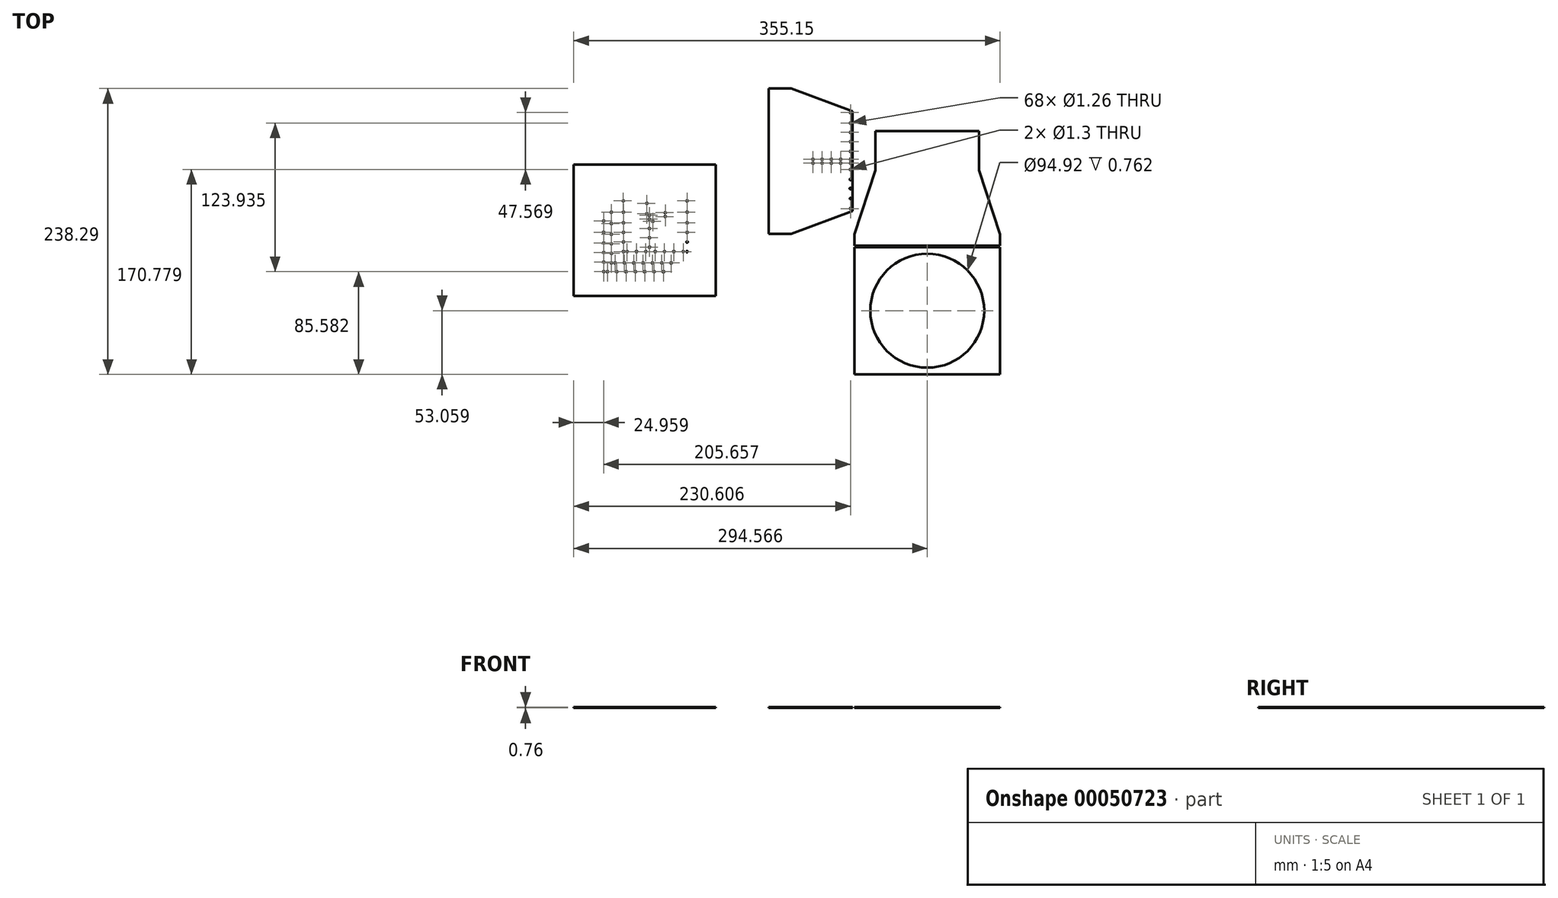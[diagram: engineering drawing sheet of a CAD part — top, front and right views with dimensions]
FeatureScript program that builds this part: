
annotation { "Feature Type Name" : "Feature", "Feature Type Description" : "" }
export const myFeature = defineFeature(function(context is Context, id is Id, definition is map)
    precondition{}
    {
        {
            var Q0;
            Q0=qCreatedBy(makeId("Top.planeOp"),FACE);
            var sketch = newSketch(context, id + "F0", { "sketchPlane" : qUnion([Q0])});
            skLineSegment(sketch, "E0", {"start": v(-23.3, 100.74) * mm, "end": v(-23.3, 17.43) * mm});
            skLineSegment(sketch, "E1", {"start": v(-93.15, 119.66) * mm, "end": v(-93.15, -1.5) * mm});
            skLineSegment(sketch, "E2", {"start": v(-74.2, -1.5) * mm, "end": v(-23.3, 17.43) * mm});
            skLineSegment(sketch, "E3", {"start": v(-74.2, 119.66) * mm, "end": v(-23.3, 100.74) * mm});
            skLineSegment(sketch, "E4", {"start": v(-21.54, -118.63) * mm, "end": v(99.62, -118.63) * mm});
            skLineSegment(sketch, "E5", {"start": v(-21.54, -12.5) * mm, "end": v(99.62, -12.5) * mm});
            skCircle(sketch, "E6", {"center": v(39.04, -65.57) * mm, "radius": 47.46 * mm});
            skLineSegment(sketch, "E7", {"start": v(-21.54, -118.63) * mm, "end": v(-21.54, -12.5) * mm});
            skLineSegment(sketch, "E8", {"start": v(99.62, -12.5) * mm, "end": v(99.62, -118.63) * mm});
            skCircle(sketch, "E9.MirrorC", {"center": v(-214.07, -16.26) * mm, "radius": 0.63 * mm});
            skCircle(sketch, "E10.MirrorC", {"center": v(-192.54, 13.97) * mm, "radius": 0.63 * mm});
            skCircle(sketch, "E11.MirrorC", {"center": v(-214.2, 26.04) * mm, "radius": 0.63 * mm});
            skCircle(sketch, "E12.MirrorC", {"center": v(-214.16, 16.65) * mm, "radius": 0.63 * mm});
            skCircle(sketch, "E13.MirrorC", {"center": v(-214.11, -0.26) * mm, "radius": 0.63 * mm});
            skCircle(sketch, "E14.MirrorC", {"center": v(-214.14, 7.74) * mm, "radius": 0.63 * mm});
            skCircle(sketch, "E15.MirrorC", {"center": v(-214.09, -8.26) * mm, "radius": 0.63 * mm});
            skCircle(sketch, "E16", {"center": v(-161.1, -16.26) * mm, "radius": 0.64 * mm});
            skCircle(sketch, "E17", {"center": v(-161.1, -8.26) * mm, "radius": 0.64 * mm});
            skCircle(sketch, "E18.MirrorC", {"center": v(-33.1, 57.5) * mm, "radius": 0.63 * mm});
            skCircle(sketch, "E19.MirrorC", {"center": v(-161.1, 26.04) * mm, "radius": 0.63 * mm});
            skCircle(sketch, "E20.MirrorC", {"center": v(-161.1, 7.74) * mm, "radius": 0.63 * mm});
            skCircle(sketch, "E21.MirrorC", {"center": v(-161.1, 16.65) * mm, "radius": 0.63 * mm});
            skCircle(sketch, "E22.MirrorC", {"center": v(-161.1, -0.26) * mm, "radius": 0.63 * mm});
            skLineSegment(sketch, "E23", {"start": v(-158.15, 37.72) * mm, "end": v(-217.13, 37.72) * mm});
            skCircle(sketch, "E24.MirrorC", {"center": v(-164.28, -16.26) * mm, "radius": 0.63 * mm});
            skCircle(sketch, "E25.MirrorC", {"center": v(-172.1, -16.26) * mm, "radius": 0.63 * mm});
            skCircle(sketch, "E26.MirrorC", {"center": v(-179.94, -16.26) * mm, "radius": 0.63 * mm});
            skCircle(sketch, "E27.MirrorC", {"center": v(-187.7, -16.26) * mm, "radius": 0.63 * mm});
            skCircle(sketch, "E28.MirrorC", {"center": v(-195.48, -16.26) * mm, "radius": 0.63 * mm});
            skCircle(sketch, "E29.MirrorC", {"center": v(-203.25, -16.26) * mm, "radius": 0.63 * mm});
            skCircle(sketch, "E30.MirrorC", {"center": v(-211.03, -16.26) * mm, "radius": 0.63 * mm});
            skCircle(sketch, "E31.MirrorC", {"center": v(-192.54, 10.77) * mm, "radius": 0.63 * mm});
            skCircle(sketch, "E32.MirrorC", {"center": v(-192.54, 3) * mm, "radius": 0.63 * mm});
            skCircle(sketch, "E33.MirrorC", {"center": v(-192.4, -4.77) * mm, "radius": 0.63 * mm});
            skCircle(sketch, "E34.MirrorC", {"center": v(-192.4, -12.54) * mm, "radius": 0.63 * mm});
            skCircle(sketch, "E35.MirrorC", {"center": v(-194.53, 24) * mm, "radius": 0.63 * mm});
            skCircle(sketch, "E36.MirrorC", {"center": v(-194.53, 15.27) * mm, "radius": 0.63 * mm});
            skCircle(sketch, "E37.MirrorC", {"center": v(-33.1, 60.68) * mm, "radius": 0.63 * mm});
            skLineSegment(sketch, "E38", {"start": v(-158.15, -17.75) * mm, "end": v(-158.15, 37.72) * mm});
            skLineSegment(sketch, "E39", {"start": v(-213, 34.35) * mm, "end": v(-162.28, 34.35) * mm});
            skLineSegment(sketch, "E40", {"start": v(-158.9, 37.72) * mm, "end": v(-158.9, -17.75) * mm});
            skLineSegment(sketch, "E41", {"start": v(-162.28, 34.35) * mm, "end": v(-162.28, -14.38) * mm});
            skLineSegment(sketch, "E42", {"start": v(-159.9, 37.72) * mm, "end": v(-159.9, -17.75) * mm});
            skLineSegment(sketch, "E43", {"start": v(-24.92, 99.72) * mm, "end": v(-23.3, 99.72) * mm});
            skLineSegment(sketch, "E44", {"start": v(-24.92, 99.72) * mm, "end": v(-24.92, 101.35) * mm});
            skLineSegment(sketch, "E45", {"start": v(-21.54, -11.3) * mm, "end": v(99.62, -11.3) * mm});
            skLineSegment(sketch, "E46", {"start": v(-4.14, 84.24) * mm, "end": v(82.22, 84.24) * mm});
            skLineSegment(sketch, "E47", {"start": v(-4.14, 51.49) * mm, "end": v(-4.14, 84.24) * mm});
            skLineSegment(sketch, "E48", {"start": v(82.22, 84.24) * mm, "end": v(82.22, 51.49) * mm});
            skCircle(sketch, "E49.MirrorC", {"center": v(-224.12, -25.75) * mm, "radius": 0.63 * mm});
            skCircle(sketch, "E50.MirrorC", {"center": v(-224.25, 16.55) * mm, "radius": 0.63 * mm});
            skCircle(sketch, "E51.MirrorC", {"center": v(-224.22, 7.16) * mm, "radius": 0.63 * mm});
            skCircle(sketch, "E52.MirrorC", {"center": v(-224.17, -9.75) * mm, "radius": 0.63 * mm});
            skCircle(sketch, "E53.MirrorC", {"center": v(-224.2, -1.75) * mm, "radius": 0.63 * mm});
            skCircle(sketch, "E54.MirrorC", {"center": v(-224.14, -17.75) * mm, "radius": 0.63 * mm});
            skCircle(sketch, "E55.MirrorC", {"center": v(-174.33, -25.75) * mm, "radius": 0.63 * mm});
            skCircle(sketch, "E56.MirrorC", {"center": v(-182.15, -25.75) * mm, "radius": 0.63 * mm});
            skCircle(sketch, "E57.MirrorC", {"center": v(-190, -25.75) * mm, "radius": 0.63 * mm});
            skCircle(sketch, "E58.MirrorC", {"center": v(-197.76, -25.75) * mm, "radius": 0.63 * mm});
            skCircle(sketch, "E59.MirrorC", {"center": v(-205.54, -25.75) * mm, "radius": 0.63 * mm});
            skCircle(sketch, "E60.MirrorC", {"center": v(-213.3, -25.75) * mm, "radius": 0.63 * mm});
            skCircle(sketch, "E61.MirrorC", {"center": v(-221.08, -25.75) * mm, "radius": 0.63 * mm});
            skCircle(sketch, "E62.MirrorC", {"center": v(-230.45, -33.05) * mm, "radius": 0.63 * mm});
            skCircle(sketch, "E63.MirrorC", {"center": v(-230.57, 9.25) * mm, "radius": 0.63 * mm});
            skCircle(sketch, "E64.MirrorC", {"center": v(-230.54, -0.14) * mm, "radius": 0.63 * mm});
            skCircle(sketch, "E65.MirrorC", {"center": v(-230.5, -17.05) * mm, "radius": 0.63 * mm});
            skCircle(sketch, "E66.MirrorC", {"center": v(-230.52, -9.04) * mm, "radius": 0.63 * mm});
            skCircle(sketch, "E67.MirrorC", {"center": v(-230.47, -25.05) * mm, "radius": 0.63 * mm});
            skCircle(sketch, "E68.MirrorC", {"center": v(-180.66, -33.05) * mm, "radius": 0.63 * mm});
            skCircle(sketch, "E69.MirrorC", {"center": v(-188.47, -33.05) * mm, "radius": 0.63 * mm});
            skCircle(sketch, "E70.MirrorC", {"center": v(-196.32, -33.05) * mm, "radius": 0.63 * mm});
            skCircle(sketch, "E71.MirrorC", {"center": v(-204.09, -33.05) * mm, "radius": 0.63 * mm});
            skCircle(sketch, "E72.MirrorC", {"center": v(-211.86, -33.05) * mm, "radius": 0.63 * mm});
            skCircle(sketch, "E73.MirrorC", {"center": v(-219.63, -33.05) * mm, "radius": 0.63 * mm});
            skCircle(sketch, "E74.MirrorC", {"center": v(-227.4, -33.05) * mm, "radius": 0.63 * mm});
            skCircle(sketch, "E75.MirrorC", {"center": v(-24.91, 19.56) * mm, "radius": 0.63 * mm});
            skCircle(sketch, "E76.MirrorC", {"center": v(-24.92, 27.96) * mm, "radius": 0.63 * mm});
            skCircle(sketch, "E77.MirrorC", {"center": v(-24.92, 36.38) * mm, "radius": 0.68 * mm});
            skCircle(sketch, "E78.MirrorC", {"center": v(-24.92, 43.92) * mm, "radius": 0.67 * mm});
            skCircle(sketch, "E79.MirrorC", {"center": v(-24.92, 52.15) * mm, "radius": 0.65 * mm});
            skCircle(sketch, "E80.MirrorC", {"center": v(-24.92, 60.68) * mm, "radius": 0.63 * mm});
            skCircle(sketch, "E81.MirrorC", {"center": v(-24.92, 67.28) * mm, "radius": 0.63 * mm});
            skCircle(sketch, "E82.MirrorC", {"center": v(-24.92, 90.89) * mm, "radius": 0.63 * mm});
            skCircle(sketch, "E83.MirrorC", {"center": v(-24.92, 99.72) * mm, "radius": 0.65 * mm});
            skCircle(sketch, "E84.MirrorC", {"center": v(-24.92, 75.4) * mm, "radius": 0.63 * mm});
            skCircle(sketch, "E85.MirrorC", {"center": v(-24.92, 83.2) * mm, "radius": 0.63 * mm});
            skCircle(sketch, "E86.MirrorC", {"center": v(-40.85, 57.5) * mm, "radius": 0.63 * mm});
            skCircle(sketch, "E87.MirrorC", {"center": v(-40.85, 60.68) * mm, "radius": 0.63 * mm});
            skCircle(sketch, "E88.MirrorC", {"center": v(-48.6, 57.5) * mm, "radius": 0.63 * mm});
            skCircle(sketch, "E89.MirrorC", {"center": v(-48.6, 60.68) * mm, "radius": 0.63 * mm});
            skCircle(sketch, "E90.MirrorC", {"center": v(-24.92, 57.5) * mm, "radius": 0.63 * mm});
            skCircle(sketch, "E91.MirrorC", {"center": v(-189.63, 8.98) * mm, "radius": 0.63 * mm});
            skLineSegment(sketch, "E92", {"start": v(-24.92, 57.5) * mm, "end": v(-24.92, 60.68) * mm});
            skLineSegment(sketch, "E93", {"start": v(-48.75, 59.08) * mm, "end": v(-56.48, 59.08) * mm});
            skCircle(sketch, "E94.MirrorC", {"center": v(-179.25, 12.95) * mm, "radius": 0.63 * mm});
            skCircle(sketch, "E95.MirrorC", {"center": v(-179.25, 16.14) * mm, "radius": 0.63 * mm});
            skCircle(sketch, "E96.MirrorC", {"center": v(-56.16, 57.5) * mm, "radius": 0.63 * mm});
            skCircle(sketch, "E97.MirrorC", {"center": v(-56.16, 60.68) * mm, "radius": 0.63 * mm});
            skLineSegment(sketch, "E98", {"start": v(-93.15, 119.66) * mm, "end": v(-74.2, 119.66) * mm});
            skLineSegment(sketch, "E99", {"start": v(-93.15, -1.5) * mm, "end": v(-74.2, -1.5) * mm});
            skLineSegment(sketch, "E100", {"start": v(-61.4, 114.9) * mm, "end": v(-61.4, 3.26) * mm});
            skLineSegment(sketch, "E101", {"start": v(-60.8, 59.08) * mm, "end": v(-56.48, 59.08) * mm});
            skLineSegment(sketch, "E102", {"start": v(-48.6, 60.68) * mm, "end": v(-48.6, 57.5) * mm});
            skLineSegment(sketch, "E103", {"start": v(-4.14, 51.49) * mm, "end": v(82.22, 51.49) * mm});
            skLineSegment(sketch, "E104", {"start": v(-4.14, 51.49) * mm, "end": v(-21.54, -1.9) * mm});
            skLineSegment(sketch, "E105", {"start": v(82.22, 51.49) * mm, "end": v(99.62, -1.9) * mm});
            skLineSegment(sketch, "E106", {"start": v(99.62, -1.9) * mm, "end": v(99.62, -11.3) * mm});
            skLineSegment(sketch, "E107", {"start": v(-21.54, -1.9) * mm, "end": v(-21.54, -11.3) * mm});
            skLineSegment(sketch, "E108", {"start": v(-255.53, 56.22) * mm, "end": v(-255.53, -53.25) * mm});
            skLineSegment(sketch, "E109", {"start": v(-255.53, -53.25) * mm, "end": v(-137.07, -53.25) * mm});
            skLineSegment(sketch, "E110", {"start": v(-137.07, -53.25) * mm, "end": v(-137.07, 56.22) * mm});
            skLineSegment(sketch, "E111", {"start": v(-137.07, 56.22) * mm, "end": v(-255.53, 56.22) * mm});
            skSolve(sketch);
        }
        {
            var Q0;
            Q0 = qSketchRegion(id + "F0", true);
            extrude(context, id + "F1", {"entities" : qUnion([Q0]), "depth" : 0.76 * mm, "offsetDistance" : 25.4 * mm});
        }
    });
